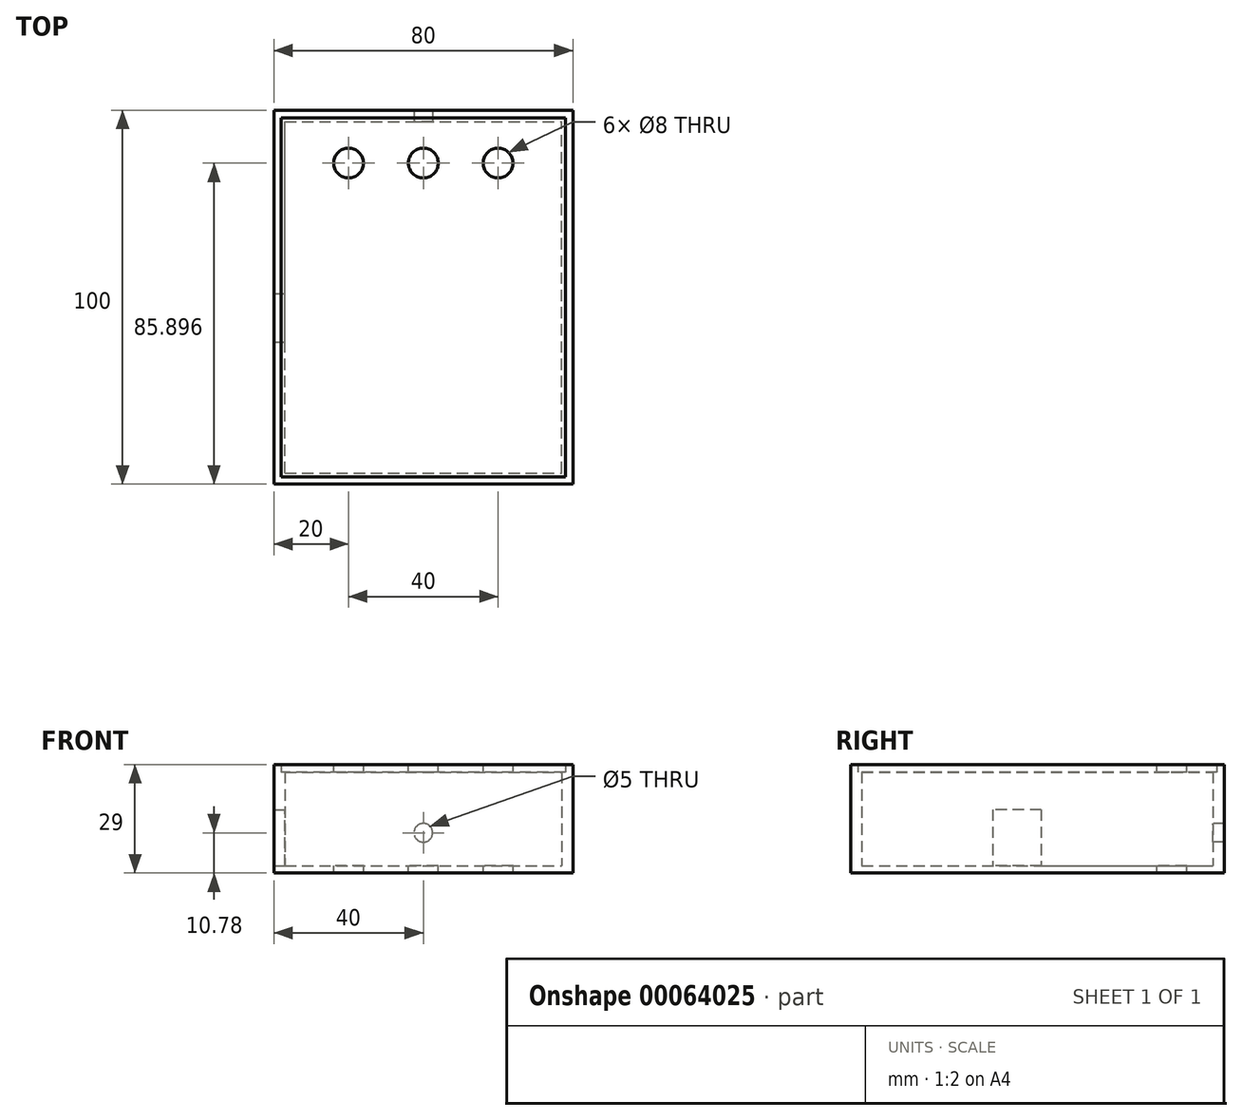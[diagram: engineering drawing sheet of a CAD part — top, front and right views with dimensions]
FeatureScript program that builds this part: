
annotation { "Feature Type Name" : "Feature", "Feature Type Description" : "" }
export const myFeature = defineFeature(function(context is Context, id is Id, definition is map)
    precondition{}
    {
        {
            var Q0;
            Q0=qCreatedBy(makeId("Top.planeOp"),FACE);
            var sketch = newSketch(context, id + "F0", { "sketchPlane" : qUnion([Q0])});
            skLineSegment(sketch, "E0.bottom", {"start": v(0, 0) * mm, "end": v(80, 0) * mm});
            skLineSegment(sketch, "E0.top", {"start": v(0, 100) * mm, "end": v(80, 100) * mm});
            skLineSegment(sketch, "E0.left", {"start": v(0, 0) * mm, "end": v(0, 100) * mm});
            skLineSegment(sketch, "E0.right", {"start": v(80, 0) * mm, "end": v(80, 100) * mm});
            skSolve(sketch);
        }
        {
            var Q0;
            Q0=makeQuery(id+"F0.imprint","IMPRINT",FACE,{"disambiguationData":[TD([[makeQuery(id+"F0.imprint","IMPRINT",EDGE,{"derivedFrom":sQuery(id+"F0.wireOp",EDGE,"E0.bottom")}),1.0]])]});
            extrude(context, id + "F1", {"entities" : qUnion([Q0]), "depth" : 2 * mm});
        }
        {
            var Q0;
            Q0=makeQuery(id+"F1.opExtrude","CAP_FACE",FACE,{"disambiguationData":[OSD([sQuery(id+"F0.wireOp",EDGE,"E0.bottom"),sQuery(id+"F0.wireOp",EDGE,"E0.top"),sQuery(id+"F0.wireOp",EDGE,"E0.left"),sQuery(id+"F0.wireOp",EDGE,"E0.right")])],"isStart":false});
            var sketch = newSketch(context, id + "F2", { "sketchPlane" : qUnion([Q0])});
            skPoint(sketch, "E1", {"position": v(3, 3) * mm});
            skPoint(sketch, "E2", {"position": v(77, 97) * mm});
            skLineSegment(sketch, "E3.bottom", {"start": v(3, 3) * mm, "end": v(77, 3) * mm});
            skLineSegment(sketch, "E3.top", {"start": v(3, 97) * mm, "end": v(77, 97) * mm});
            skLineSegment(sketch, "E3.left", {"start": v(3, 3) * mm, "end": v(3, 97) * mm});
            skLineSegment(sketch, "E3.right", {"start": v(77, 3) * mm, "end": v(77, 97) * mm});
            skLineSegment(sketch, "E4.bottom", {"start": v(0, 0) * mm, "end": v(80, 0) * mm});
            skLineSegment(sketch, "E4.top", {"start": v(0, 100) * mm, "end": v(80, 100) * mm});
            skLineSegment(sketch, "E4.left", {"start": v(0, 0) * mm, "end": v(0, 100) * mm});
            skLineSegment(sketch, "E4.right", {"start": v(80, 0) * mm, "end": v(80, 100) * mm});
            skSolve(sketch);
        }
        {
            var Q0;
            Q0=makeQuery(id+"F2.imprint","IMPRINT",FACE,{"disambiguationData":[TD([[makeQuery(id+"F2.imprint","IMPRINT",EDGE,{"derivedFrom":sQuery(id+"F2.wireOp",EDGE,"E3.bottom")}),-1.0]])]});
            extrude(context, id + "F3", {"entities" : qUnion([Q0]), "operationType" : NewBodyOperationType.ADD, "depth" : 25 * mm});
        }
        {
            var Q0;
            Q0=makeQuery(id+"F3.opExtrude","SWEPT_FACE",FACE,{"disambiguationData":[OSD([sQuery(id+"F2.wireOp",EDGE,"E3.left")])]});
            var sketch = newSketch(context, id + "F4", { "sketchPlane" : qUnion([Q0])});
            skPoint(sketch, "E5", {"position": v(38, 2) * mm});
            skPoint(sketch, "E6", {"position": v(51, 17) * mm});
            skLineSegment(sketch, "E7.bottom", {"start": v(38, 2) * mm, "end": v(51, 2) * mm});
            skLineSegment(sketch, "E7.top", {"start": v(38, 17) * mm, "end": v(51, 17) * mm});
            skLineSegment(sketch, "E7.left", {"start": v(38, 2) * mm, "end": v(38, 17) * mm});
            skLineSegment(sketch, "E7.right", {"start": v(51, 2) * mm, "end": v(51, 17) * mm});
            skSolve(sketch);
        }
        {
            var Q0;
            Q0=makeQuery(id+"F4.imprint","IMPRINT",FACE,{"disambiguationData":[TD([[makeQuery(id+"F4.imprint","IMPRINT",EDGE,{"derivedFrom":sQuery(id+"F4.wireOp",EDGE,"E7.bottom")}),1.0]])]});
            extrude(context, id + "F5", {"entities" : qUnion([Q0]), "operationType" : NewBodyOperationType.REMOVE, "endBound" : BoundingType.THROUGH_ALL, "oppositeDirection" : true, "depth" : 25 * mm});
        }
        {
            var Q0;
            Q0=makeQuery(id+"F3.opExtrude","CAP_FACE",FACE,{"disambiguationData":[OSD([sQuery(id+"F2.wireOp",EDGE,"E3.bottom"),sQuery(id+"F2.wireOp",EDGE,"E3.top"),sQuery(id+"F2.wireOp",EDGE,"E3.left"),sQuery(id+"F2.wireOp",EDGE,"E3.right"),sQuery(id+"F2.wireOp",EDGE,"E4.bottom"),sQuery(id+"F2.wireOp",EDGE,"E4.top"),sQuery(id+"F2.wireOp",EDGE,"E4.left"),sQuery(id+"F2.wireOp",EDGE,"E4.right")])],"isStart":false});
            var sketch = newSketch(context, id + "F6", { "sketchPlane" : qUnion([Q0])});
            skPoint(sketch, "E8", {"position": v(2, 2) * mm});
            skPoint(sketch, "E9", {"position": v(78, 98) * mm});
            skLineSegment(sketch, "E10.bottom", {"start": v(0, 0) * mm, "end": v(80, 0) * mm});
            skLineSegment(sketch, "E10.top", {"start": v(0, 100) * mm, "end": v(80, 100) * mm});
            skLineSegment(sketch, "E10.left", {"start": v(0, 0) * mm, "end": v(0, 100) * mm});
            skLineSegment(sketch, "E10.right", {"start": v(80, 0) * mm, "end": v(80, 100) * mm});
            skLineSegment(sketch, "E11.bottom", {"start": v(78, 98) * mm, "end": v(2, 98) * mm});
            skLineSegment(sketch, "E11.top", {"start": v(78, 2) * mm, "end": v(2, 2) * mm});
            skLineSegment(sketch, "E11.left", {"start": v(78, 98) * mm, "end": v(78, 2) * mm});
            skLineSegment(sketch, "E11.right", {"start": v(2, 98) * mm, "end": v(2, 2) * mm});
            skSolve(sketch);
        }
        {
            var Q0;
            Q0=makeQuery(id+"F6.imprint","IMPRINT",FACE,{"disambiguationData":[TD([[makeQuery(id+"F6.imprint","IMPRINT",EDGE,{"derivedFrom":sQuery(id+"F6.wireOp",EDGE,"E10.bottom")}),1.0]])]});
            extrude(context, id + "F7", {"entities" : qUnion([Q0]), "operationType" : NewBodyOperationType.ADD, "depth" : 2 * mm});
        }
        {
            var Q0;
            Q0=makeQuery(id+"F3.opExtrude","CAP_FACE",FACE,{"disambiguationData":[OSD([sQuery(id+"F2.wireOp",EDGE,"E3.bottom"),sQuery(id+"F2.wireOp",EDGE,"E3.top"),sQuery(id+"F2.wireOp",EDGE,"E3.left"),sQuery(id+"F2.wireOp",EDGE,"E3.right"),sQuery(id+"F2.wireOp",EDGE,"E4.bottom"),sQuery(id+"F2.wireOp",EDGE,"E4.top"),sQuery(id+"F2.wireOp",EDGE,"E4.left"),sQuery(id+"F2.wireOp",EDGE,"E4.right")])],"isStart":false});
            var sketch = newSketch(context, id + "F8", { "sketchPlane" : qUnion([Q0])});
            skLineSegment(sketch, "E12.bottom", {"start": v(2, 98) * mm, "end": v(78, 98) * mm});
            skLineSegment(sketch, "E12.top", {"start": v(2, 2) * mm, "end": v(78, 2) * mm});
            skLineSegment(sketch, "E12.left", {"start": v(2, 98) * mm, "end": v(2, 2) * mm});
            skLineSegment(sketch, "E12.right", {"start": v(78, 98) * mm, "end": v(78, 2) * mm});
            skSolve(sketch);
        }
        {
            var Q0;
            Q0 = qSketchRegion(id + "F8", true);
            extrude(context, id + "F9", {"entities" : qUnion([Q0]), "depth" : 2 * mm});
        }
        {
            var Q0;
            Q0=makeQuery(id+"F3.opExtrude","SWEPT_FACE",FACE,{"disambiguationData":[OSD([sQuery(id+"F2.wireOp",EDGE,"E3.top")])]});
            var sketch = newSketch(context, id + "F10", { "sketchPlane" : qUnion([Q0])});
            skPoint(sketch, "E13", {"position": v(40, 10.78) * mm});
            skPoint(sketch, "E13.positionSnap0", {"position": v(40, 2) * mm});
            skCircle(sketch, "E14", {"center": v(40, 10.78) * mm, "radius": 2.5 * mm});
            skSolve(sketch);
        }
        {
            var Q0;
            Q0=makeQuery(id+"F10.imprint","IMPRINT",FACE,{"disambiguationData":[TD([[makeQuery(id+"F10.imprint","IMPRINT",EDGE,{"derivedFrom":sQuery(id+"F10.wireOp",EDGE,"E14")}),1.0]])]});
            extrude(context, id + "F11", {"entities" : qUnion([Q0]), "operationType" : NewBodyOperationType.REMOVE, "endBound" : BoundingType.THROUGH_ALL, "oppositeDirection" : true, "depth" : 25 * mm});
        }
        {
            var Q0;
            Q0=makeQuery(id+"F9.opExtrude","CAP_FACE",FACE,{"disambiguationData":[OSD([sQuery(id+"F8.wireOp",EDGE,"E12.bottom"),sQuery(id+"F8.wireOp",EDGE,"E12.top"),sQuery(id+"F8.wireOp",EDGE,"E12.left"),sQuery(id+"F8.wireOp",EDGE,"E12.right")])],"isStart":false});
            var sketch = newSketch(context, id + "F12", { "sketchPlane" : qUnion([Q0])});
            skPoint(sketch, "E15", {"position": v(40, 85.9) * mm});
            skPoint(sketch, "E15.positionSnap0", {"position": v(40, 98) * mm});
            skPoint(sketch, "E16", {"position": v(20, 85.9) * mm});
            skPoint(sketch, "E17", {"position": v(60, 85.9) * mm});
            skCircle(sketch, "E18", {"center": v(40, 85.9) * mm, "radius": 4 * mm});
            skCircle(sketch, "E19", {"center": v(60, 85.9) * mm, "radius": 4 * mm});
            skCircle(sketch, "E20", {"center": v(20, 85.9) * mm, "radius": 4 * mm});
            skSolve(sketch);
        }
        {
            var Q0;
            Q0=makeQuery(id+"F12.imprint","IMPRINT",FACE,{"disambiguationData":[TD([[makeQuery(id+"F12.imprint","IMPRINT",EDGE,{"derivedFrom":sQuery(id+"F12.wireOp",EDGE,"E20")}),1.0]])]});
            var Q1;
            Q1=makeQuery(id+"F12.imprint","IMPRINT",FACE,{"disambiguationData":[TD([[makeQuery(id+"F12.imprint","IMPRINT",EDGE,{"derivedFrom":sQuery(id+"F12.wireOp",EDGE,"E18")}),1.0]])]});
            var Q2;
            Q2=makeQuery(id+"F12.imprint","IMPRINT",FACE,{"disambiguationData":[TD([[makeQuery(id+"F12.imprint","IMPRINT",EDGE,{"derivedFrom":sQuery(id+"F12.wireOp",EDGE,"E19")}),1.0]])]});
            extrude(context, id + "F13", {"entities" : qUnion([Q0, Q1, Q2]), "operationType" : NewBodyOperationType.REMOVE, "endBound" : BoundingType.THROUGH_ALL, "oppositeDirection" : true, "depth" : 25 * mm});
        }
    });
